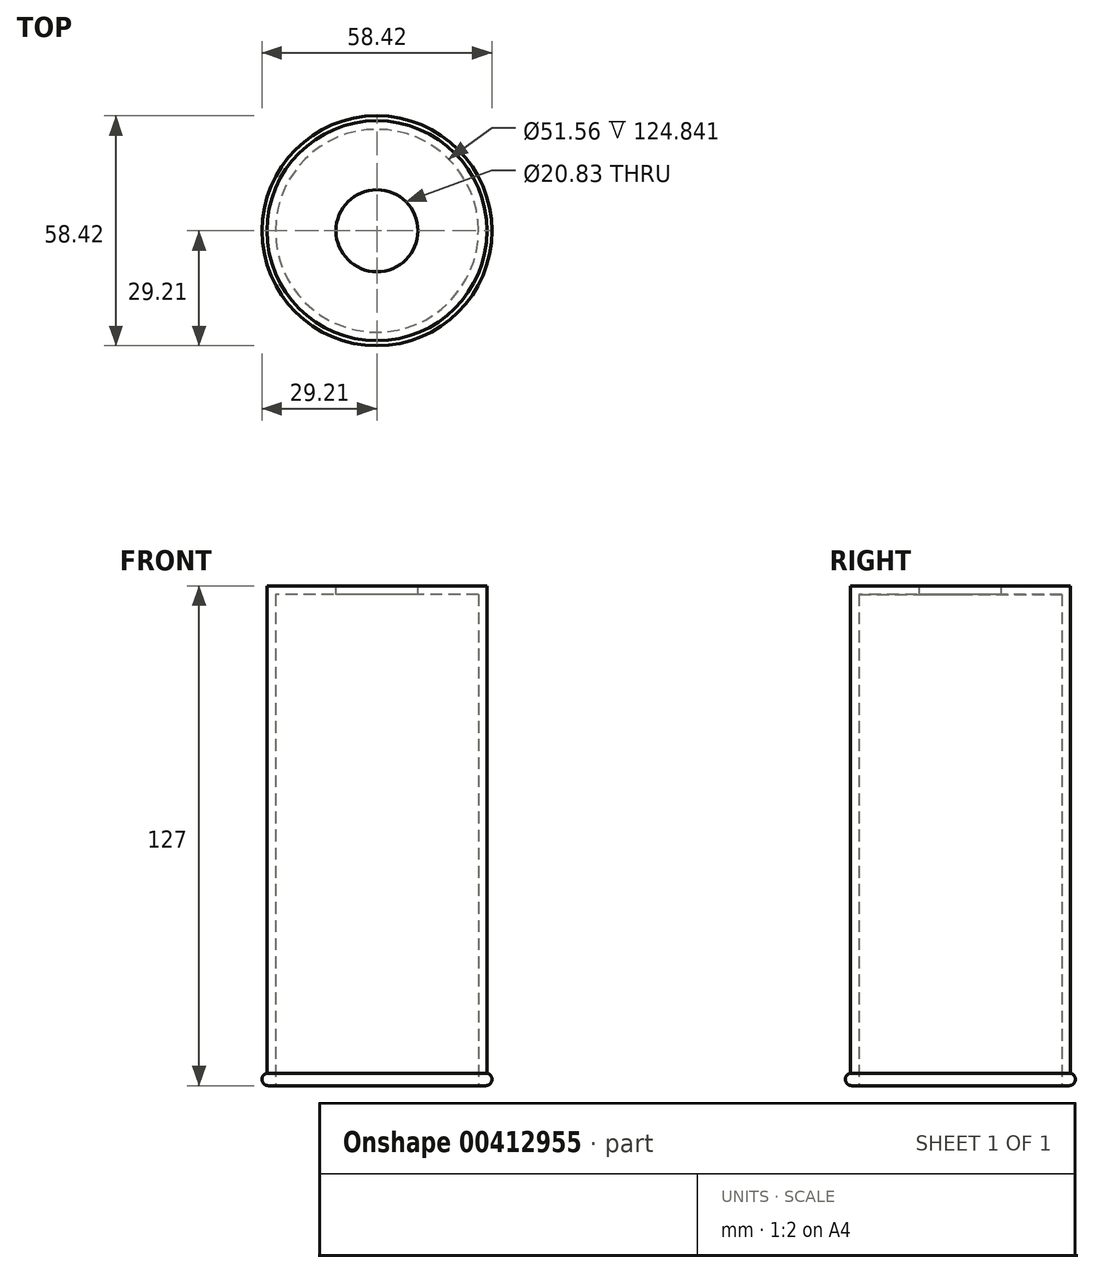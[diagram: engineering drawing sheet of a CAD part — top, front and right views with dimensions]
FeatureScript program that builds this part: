
annotation { "Feature Type Name" : "Feature", "Feature Type Description" : "" }
export const myFeature = defineFeature(function(context is Context, id is Id, definition is map)
    precondition{}
    {
        {
            var Q0;
            Q0=qCreatedBy(makeId("Top.planeOp"),FACE);
            var sketch = newSketch(context, id + "F0", { "sketchPlane" : qUnion([Q0])});
            skCircle(sketch, "E0", {"center": v(0, 0) * mm, "radius": 27.94 * mm});
            skSolve(sketch);
        }
        {
            var Q0;
            Q0 = qSketchRegion(id + "F0", true);
            extrude(context, id + "F1", {"entities" : qUnion([Q0]), "depth" : 127 * mm});
        }
        {
            var Q0;
            Q0=qCreatedBy(makeId("Top.planeOp"),FACE);
            var sketch = newSketch(context, id + "F2", { "sketchPlane" : qUnion([Q0])});
            skCircle(sketch, "E1", {"center": v(0, 0) * mm, "radius": 29.2 * mm});
            skSolve(sketch);
        }
        {
            var Q0;
            Q0 = qSketchRegion(id + "F2", true);
            extrude(context, id + "F3", {"entities" : qUnion([Q0]), "operationType" : NewBodyOperationType.ADD, "depth" : 3.17 * mm});
        }
        {
            var Q0;
            Q0=makeQuery(id+"F3.opExtrude","CAP_EDGE",EDGE,{"disambiguationData":[OSD([sQuery(id+"F2.wireOp",EDGE,"E1")])],"isStart":true});
            var Q1;
            Q1=makeQuery(id+"F3.opExtrude","CAP_EDGE",EDGE,{"disambiguationData":[OSD([sQuery(id+"F2.wireOp",EDGE,"E1")])],"isStart":false});
            fillet(context, id + "F4", {"entities" : qUnion([Q0, Q1]), "radius" : 1.59 * mm, "tangentPropagation" : true, "allowEdgeOverflow" : false});
        }
        {
            var Q0;
            Q0=makeQuery(id+"F3.boolean.opBoolean","MERGE",FACE,{"derivedFrom":[makeQuery(id+"F1.opExtrude","CAP_FACE",FACE,{"disambiguationData":[OSD([sQuery(id+"F0.wireOp",EDGE,"E0")])],"isStart":true}),makeQuery(id+"F3.opExtrude","CAP_FACE",FACE,{"disambiguationData":[OSD([sQuery(id+"F2.wireOp",EDGE,"E1")])],"isStart":true})]});
            shell(context, id + "F5", {"entities" : qUnion([Q0]), "thickness" : 2.16 * mm});
        }
        {
            var Q0;
            Q0=makeQuery(id+"F1.opExtrude","CAP_FACE",FACE,{"disambiguationData":[OSD([sQuery(id+"F0.wireOp",EDGE,"E0")])],"isStart":false});
            var sketch = newSketch(context, id + "F6", { "sketchPlane" : qUnion([Q0])});
            skCircle(sketch, "E2", {"center": v(0, 0) * mm, "radius": 10.41 * mm});
            skSolve(sketch);
        }
        {
            var Q0;
            Q0 = qSketchRegion(id + "F6", true);
            extrude(context, id + "F7", {"entities" : qUnion([Q0]), "operationType" : NewBodyOperationType.REMOVE, "endBound" : BoundingType.THROUGH_ALL, "oppositeDirection" : true, "depth" : 25.4 * mm});
        }
    });
